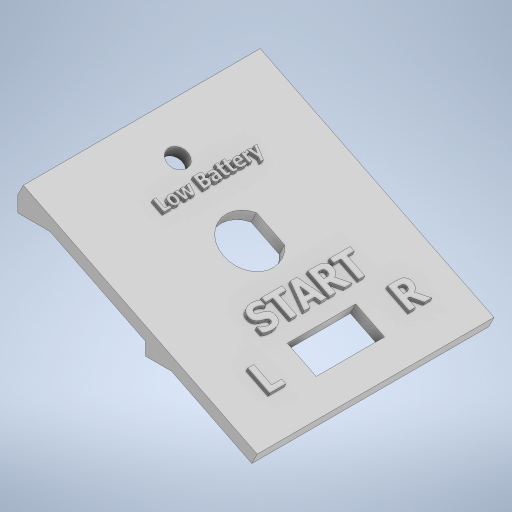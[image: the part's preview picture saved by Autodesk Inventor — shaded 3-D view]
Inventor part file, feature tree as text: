
AUTODESK INVENTOR PART (.ipt)
format: ipt  version: 2024.2 (Build 282272000, 272)  size: 784,896 bytes
history: native  units: mm
features: sketch x7, extrude x6, projected_geometry x4, emboss x1
ambient origin geometry x8: Origin, YZ Plane, XZ Plane, XY Plane, X Axis, Y Axis, Z Axis, Center Point
bodies: Solid1 (feature_tree)
feature tree (18):
  extrude  "Extrusion1"  Depth=3.0mm
  extrude  "Extrusion2"  Depth=6.5mm
  extrude  "Extrusion3"  Depth=9.0mm TaperAngle=0.0deg
  extrude  "Extrusion5"  Depth=9.0mm TaperAngle=0.0deg
  emboss  "Emboss1"
  extrude  "Extrusion6"  Depth=15.0mm
  extrude  "Extrusion7"  Depth=13.0mm
  sketch  "Sketch2"  dims[d4=3.0mm d5=3.0mm]
  sketch  "Sketch3"  dims[d6=38.25mm d8=6.5mm]
  projected_geometry  "Projected Loop1"
  sketch  "Sketch4"  dims[d9=8.0mm d10=9.0mm d11=0.0mm]
  projected_geometry  "Projected Loop2"
  projected_geometry  "Projected Loop3"
  projected_geometry  "Projected Loop4"
  sketch  "Sketch7"  dims[d12=41.0mm d13=0.0mm d14=9.0mm d15=0.0mm]
  sketch  "Sketch8"  dims[d16=15.0mm d29=20.0mm]
  sketch  "Sketch9"  dims[d30=5.0mm d31=13.0mm]
  sketch  "Sketch10"  dims[d32=29.5mm d33=17.0mm d34=5.2mm d35=10.0mm d36=20.0mm d37=8.0mm d38=8.5mm d39=20.0mm d40=0.0mm d41=0.0mm d42=1.0mm d43=0.0mm d44=49.0mm d45=3.0mm d46=3.0mm d47=3.25mm d48=3.25mm d49=4.0mm d50=2.5mm d51=0.0mm d52=3.0mm d53=3.0mm d54=51.0mm d55=4.0mm d56=4.0mm d57=2.5mm d58=0.0mm]
